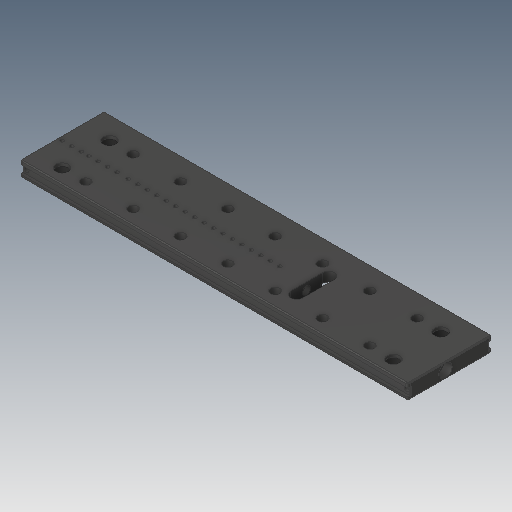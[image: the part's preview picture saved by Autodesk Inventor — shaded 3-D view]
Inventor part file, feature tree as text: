
AUTODESK INVENTOR PART (.ipt)
format: ipt  version: 2019 (Build 230136000, 136)  size: 228,864 bytes
history: native  units: mm
features: chamfer x1
ambient origin geometry x8: Origin, YZ Plane, XZ Plane, XY Plane, X Axis, Y Axis, Z Axis, Center Point
bodies: Solid1 (feature_tree)
feature tree (1):
  chamfer  "Chamfer1"  [1 undecoded]
note: 1 required parameter value undecoded (feature->parameter linkage not recoverable at this tier; creation-order binding heuristic only, values carry confidence <= 0.55)
